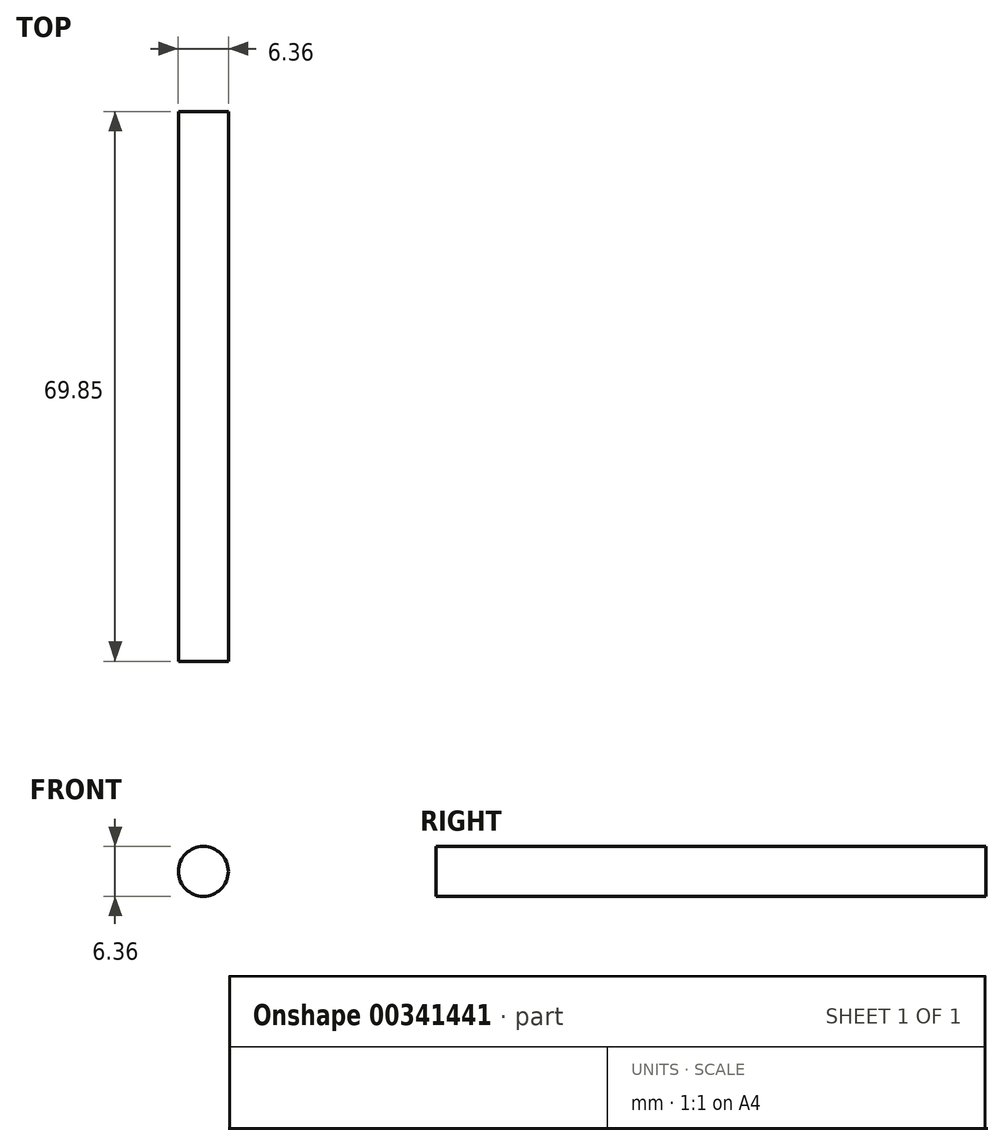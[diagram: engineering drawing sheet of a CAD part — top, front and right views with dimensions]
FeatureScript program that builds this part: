
annotation { "Feature Type Name" : "Feature", "Feature Type Description" : "" }
export const myFeature = defineFeature(function(context is Context, id is Id, definition is map)
    precondition{}
    {
        {
            var Q0;
            Q0=qCreatedBy(makeId("Front.planeOp"),FACE);
            var sketch = newSketch(context, id + "F0", { "sketchPlane" : qUnion([Q0])});
            skCircle(sketch, "E0", {"center": v(0, 0) * mm, "radius": 3.17 * mm});
            skSolve(sketch);
        }
        {
            var Q0;
            Q0 = qSketchRegion(id + "F0", true);
            extrude(context, id + "F1", {"entities" : qUnion([Q0]), "depth" : 69.85 * mm});
        }
    });
